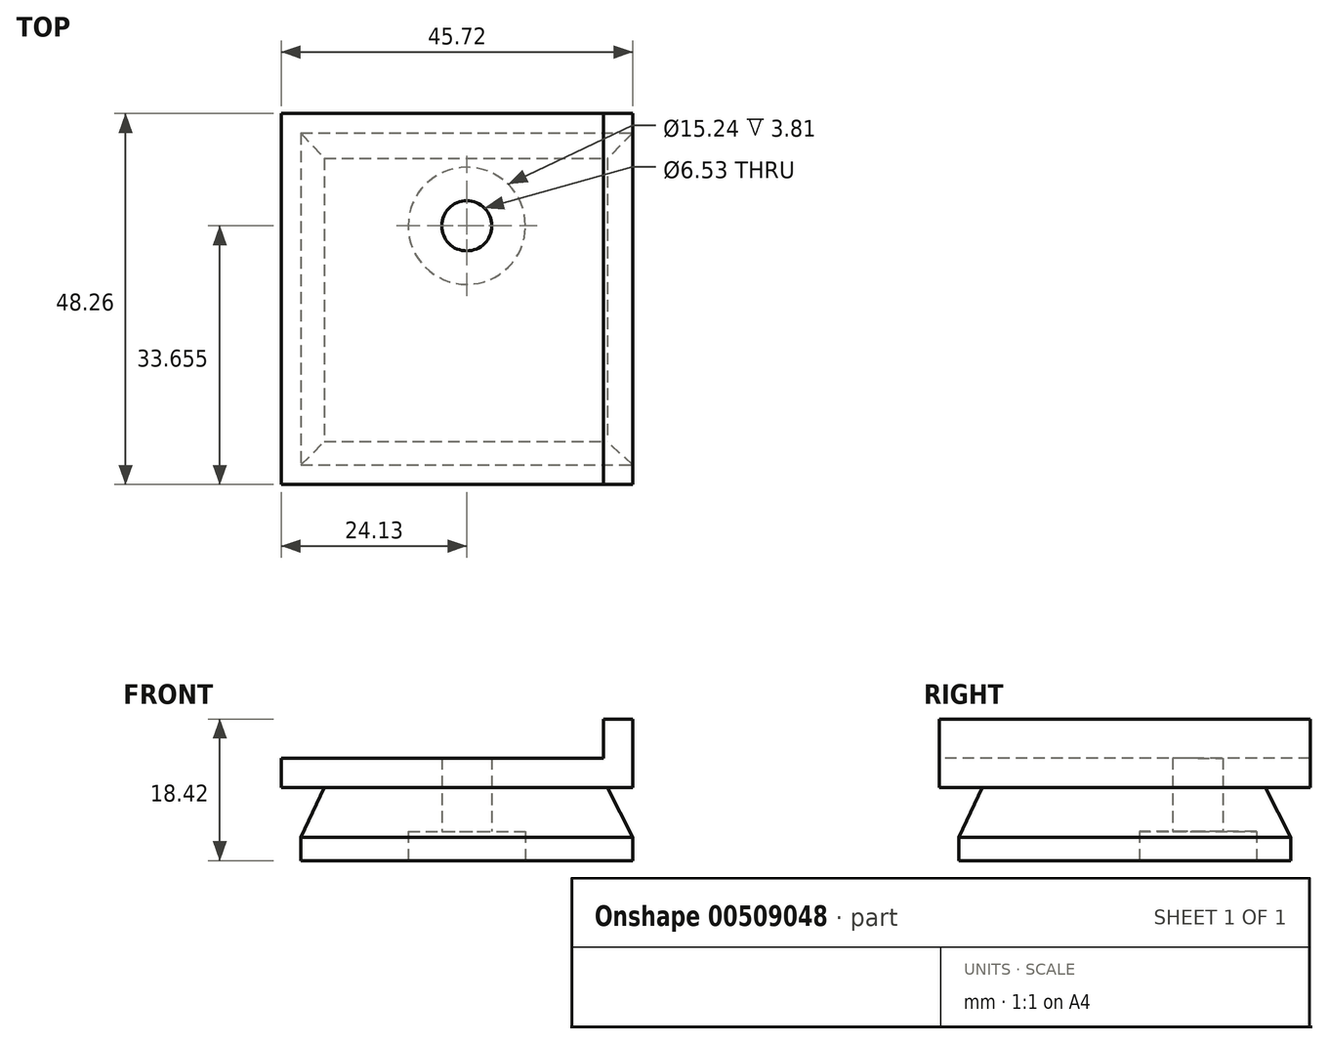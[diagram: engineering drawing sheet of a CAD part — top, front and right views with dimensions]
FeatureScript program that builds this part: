
annotation { "Feature Type Name" : "Feature", "Feature Type Description" : "" }
export const myFeature = defineFeature(function(context is Context, id is Id, definition is map)
    precondition{}
    {
        {
            var Q0;
            Q0=qCreatedBy(makeId("Top.planeOp"),FACE);
            var sketch = newSketch(context, id + "F0", { "sketchPlane" : qUnion([Q0])});
            skLineSegment(sketch, "E0.bottom", {"start": v(-21.59, 21.59) * mm, "end": v(21.59, 21.59) * mm});
            skLineSegment(sketch, "E0.top", {"start": v(-21.59, -21.6) * mm, "end": v(21.59, -21.6) * mm});
            skLineSegment(sketch, "E0.left", {"start": v(-21.59, 21.59) * mm, "end": v(-21.59, -21.6) * mm});
            skLineSegment(sketch, "E0.right", {"start": v(21.59, 21.59) * mm, "end": v(21.59, -21.6) * mm});
            skSolve(sketch);
        }
        {
            var Q0;
            Q0=qCreatedBy(makeId("Top.planeOp"),FACE);
            cPlane(context, id + "F1", {"entities" : qUnion([Q0]), "cplaneType" : CPlaneType.OFFSET, "offset" : 6.48 * mm, "width" : 152.4 * mm, "height" : 152.4 * mm});
        }
        {
            var Q0;
            Q0=qCreatedBy(id+"F1.planeOp",FACE);
            var sketch = newSketch(context, id + "F2", { "sketchPlane" : qUnion([Q0])});
            skLineSegment(sketch, "E1.0", {"start": v(21.59, 21.59) * mm, "end": v(21.59, -21.6) * mm});
            skLineSegment(sketch, "E2.0", {"start": v(-21.59, 21.59) * mm, "end": v(21.59, 21.59) * mm});
            skPoint(sketch, "E3.0", {"position": v(-21.59, 21.59) * mm});
            skLineSegment(sketch, "E4.0", {"start": v(-21.59, 21.59) * mm, "end": v(-21.59, -21.6) * mm});
            skLineSegment(sketch, "E5.0", {"start": v(-21.59, -21.6) * mm, "end": v(21.59, -21.6) * mm});
            skLineSegment(sketch, "E6.bottom", {"start": v(-18.54, 18.29) * mm, "end": v(18.29, 18.29) * mm});
            skLineSegment(sketch, "E6.top", {"start": v(-18.54, -18.54) * mm, "end": v(18.29, -18.54) * mm});
            skLineSegment(sketch, "E6.left", {"start": v(-18.54, 18.29) * mm, "end": v(-18.54, -18.54) * mm});
            skLineSegment(sketch, "E6.right", {"start": v(18.29, 18.29) * mm, "end": v(18.29, -18.54) * mm});
            skSolve(sketch);
        }
        {
            var Q0;
            Q0=makeQuery(id+"F0.imprint","IMPRINT",FACE,{"disambiguationData":[TD([[makeQuery(id+"F0.imprint","IMPRINT",EDGE,{"derivedFrom":sQuery(id+"F0.wireOp",EDGE,"E0.bottom")}),-1.0]])]});
            extrude(context, id + "F3", {"entities" : qUnion([Q0]), "oppositeDirection" : true, "depth" : 3.05 * mm, "offsetDistance" : 25.4 * mm});
        }
        {
            var Q1;
            Q1=makeQuery(id+"F3.opExtrude","CAP_FACE",FACE,{"disambiguationData":[OSD([sQuery(id+"F0.wireOp",EDGE,"E0.bottom"),sQuery(id+"F0.wireOp",EDGE,"E0.top"),sQuery(id+"F0.wireOp",EDGE,"E0.left"),sQuery(id+"F0.wireOp",EDGE,"E0.right")])],"isStart":true});
            var Q2;
            Q2=makeQuery(id+"F2.imprint","IMPRINT",FACE,{"disambiguationData":[TD([[makeQuery(id+"F2.imprint","IMPRINT",EDGE,{"derivedFrom":sQuery(id+"F2.wireOp",EDGE,"E6.bottom")}),-1.0]])]});
            loft(context, id + "F4", {"operationType" : NewBodyOperationType.ADD, "sheetProfilesArray" : [{ "sheetProfileEntities" : qUnion([Q1]) }, { "sheetProfileEntities" : qUnion([Q2]) }]});
        }
        {
            var Q0;
            Q0=makeQuery(id+"F3.opExtrude","CAP_FACE",FACE,{"disambiguationData":[OSD([sQuery(id+"F0.wireOp",EDGE,"E0.bottom"),sQuery(id+"F0.wireOp",EDGE,"E0.top"),sQuery(id+"F0.wireOp",EDGE,"E0.left"),sQuery(id+"F0.wireOp",EDGE,"E0.right")])],"isStart":false});
            var sketch = newSketch(context, id + "F5", { "sketchPlane" : qUnion([Q0])});
            skCircle(sketch, "E7", {"center": v(0, -9.53) * mm, "radius": 7.62 * mm});
            skLineSegment(sketch, "E8.0", {"start": v(-18.54, -18.29) * mm, "end": v(-18.54, 18.54) * mm});
            skLineSegment(sketch, "E9.0", {"start": v(18.29, -18.29) * mm, "end": v(-18.54, -18.29) * mm});
            skSolve(sketch);
        }
        {
            var Q0;
            Q0 = qSketchRegion(id + "F5", true);
            extrude(context, id + "F6", {"entities" : qUnion([Q0]), "operationType" : NewBodyOperationType.REMOVE, "oppositeDirection" : true, "depth" : 3.8 * mm});
        }
        {
            var Q0;
            Q0=makeQuery(id+"F6.boolean.opBoolean","COPY",FACE,{"derivedFrom":makeQuery(id+"F6.opExtrude","CAP_FACE",FACE,{"disambiguationData":[OSD([sQuery(id+"F5.wireOp",EDGE,"E7")])],"isStart":false})});
            var sketch = newSketch(context, id + "F7", { "sketchPlane" : qUnion([Q0])});
            skCircle(sketch, "E10.0", {"center": v(0, -9.53) * mm, "radius": 7.62 * mm});
            skCircle(sketch, "E11", {"center": v(0, -9.53) * mm, "radius": 3.26 * mm});
            skSolve(sketch);
        }
        {
            var Q0;
            Q0=makeQuery(id+"F7.imprint","IMPRINT",FACE,{"disambiguationData":[TD([[makeQuery(id+"F7.imprint","IMPRINT",EDGE,{"derivedFrom":sQuery(id+"F7.wireOp",EDGE,"E11")}),1.0]])]});
            extrude(context, id + "F8", {"entities" : qUnion([Q0]), "operationType" : NewBodyOperationType.REMOVE, "oppositeDirection" : true, "depth" : 25.4 * mm});
        }
        {
            var Q0;
            Q0=makeQuery(id+"F4.opLoft","CAP_FACE",FACE,{"disambiguationData":[OSD([makeQuery(id+"F2.imprint","IMPRINT",FACE,{"disambiguationData":[TD([[makeQuery(id+"F2.imprint","IMPRINT",EDGE,{"derivedFrom":sQuery(id+"F2.wireOp",EDGE,"E6.bottom")}),-1.0]])]})])],"isStart":true});
            var sketch = newSketch(context, id + "F9", { "sketchPlane" : qUnion([Q0])});
            skLineSegment(sketch, "E12.0.0", {"start": v(-18.54, 18.29) * mm, "end": v(-18.54, -18.54) * mm});
            skLineSegment(sketch, "E12.0.1", {"start": v(-18.54, -18.54) * mm, "end": v(18.29, -18.54) * mm});
            skLineSegment(sketch, "E12.0.2", {"start": v(18.29, -18.54) * mm, "end": v(18.29, 18.29) * mm});
            skLineSegment(sketch, "E12.0.3", {"start": v(18.29, 18.29) * mm, "end": v(-18.54, 18.29) * mm});
            skCircle(sketch, "E13.0", {"center": v(0, 9.53) * mm, "radius": 3.26 * mm});
            skLineSegment(sketch, "E14.0", {"start": v(-21.59, 21.59) * mm, "end": v(-21.59, -21.6) * mm});
            skLineSegment(sketch, "E15.0", {"start": v(21.59, 21.59) * mm, "end": v(21.59, -21.6) * mm});
            skLineSegment(sketch, "E16.0", {"start": v(-21.59, -21.6) * mm, "end": v(21.59, -21.6) * mm});
            skLineSegment(sketch, "E17", {"start": v(21.59, 21.59) * mm, "end": v(21.59, 24.13) * mm});
            skLineSegment(sketch, "E18", {"start": v(21.59, 24.13) * mm, "end": v(-21.59, 24.13) * mm});
            skLineSegment(sketch, "E19", {"start": v(-21.59, 24.13) * mm, "end": v(-21.59, 21.59) * mm});
            skLineSegment(sketch, "E20.bottom", {"start": v(-21.59, 24.13) * mm, "end": v(-24.13, 24.13) * mm});
            skLineSegment(sketch, "E20.top", {"start": v(-21.59, -24.13) * mm, "end": v(-24.13, -24.13) * mm});
            skLineSegment(sketch, "E20.left", {"start": v(-21.59, 24.13) * mm, "end": v(-21.59, -24.13) * mm});
            skLineSegment(sketch, "E20.right", {"start": v(-24.13, 24.13) * mm, "end": v(-24.13, -24.13) * mm});
            skLineSegment(sketch, "E21.bottom", {"start": v(-21.59, -24.13) * mm, "end": v(21.6, -24.13) * mm});
            skLineSegment(sketch, "E21.left", {"start": v(-21.59, -24.13) * mm, "end": v(-21.59, -21.6) * mm});
            skLineSegment(sketch, "E21.right", {"start": v(21.59, -24.13) * mm, "end": v(21.59, -21.6) * mm});
            skSolve(sketch);
        }
        {
            var Q0;
            Q0 = qSketchRegion(id + "F9", true);
            var Q1;
            Q1=makeQuery(id+"F9.imprint","IMPRINT",FACE,{"disambiguationData":[TD([[makeQuery(id+"F9.imprint","IMPRINT",EDGE,{"derivedFrom":sQuery(id+"F9.wireOp",EDGE,"E12.0.0")}),1.0]])]});
            extrude(context, id + "F10", {"entities" : qUnion([Q0, Q1]), "operationType" : NewBodyOperationType.ADD, "depth" : 3.8 * mm});
        }
        {
            var Q0;
            Q0=makeQuery(id+"F10.opExtrude","CAP_FACE",FACE,{"disambiguationData":[OSD([sQuery(id+"F9.wireOp",EDGE,"E13.0"),sQuery(id+"F9.wireOp",EDGE,"E14.0"),sQuery(id+"F9.wireOp",EDGE,"94784294-9462-4c30-add6-040bfe12e883.0"),sQuery(id+"F9.wireOp",EDGE,"E15.0"),sQuery(id+"F9.wireOp",EDGE,"E16.0")])],"isStart":false});
            var sketch = newSketch(context, id + "F11", { "sketchPlane" : qUnion([Q0])});
            skLineSegment(sketch, "E22.0", {"start": v(21.59, -24.13) * mm, "end": v(21.59, 24.13) * mm});
            skLineSegment(sketch, "E23.bottom", {"start": v(21.59, 24.13) * mm, "end": v(17.78, 24.13) * mm});
            skLineSegment(sketch, "E23.top", {"start": v(21.59, -24.13) * mm, "end": v(17.78, -24.13) * mm});
            skLineSegment(sketch, "E23.left", {"start": v(21.59, 24.13) * mm, "end": v(21.59, -24.13) * mm});
            skLineSegment(sketch, "E23.right", {"start": v(17.78, 24.13) * mm, "end": v(17.78, -24.13) * mm});
            skSolve(sketch);
        }
        {
            var Q0;
            Q0=makeQuery(id+"F11.imprint","IMPRINT",FACE,{"disambiguationData":[TD([[makeQuery(id+"F11.imprint","IMPRINT",EDGE,{"derivedFrom":sQuery(id+"F11.wireOp",EDGE,"ndIwKrWf-CE43-nT5V-FJ0C-8dBKbPJmRig6.bottom")}),1.0]])]});
            var Q1;
            Q1=makeQuery(id+"F11.imprint","IMPRINT",FACE,{"disambiguationData":[TD([[makeQuery(id+"F11.imprint","IMPRINT",EDGE,{"derivedFrom":sQuery(id+"F11.wireOp",EDGE,"E23.bottom")}),1.0]])]});
            extrude(context, id + "F12", {"entities" : qUnion([Q0, Q1]), "operationType" : NewBodyOperationType.ADD, "depth" : 5.08 * mm, "offsetDistance" : 25.4 * mm});
        }
    });
